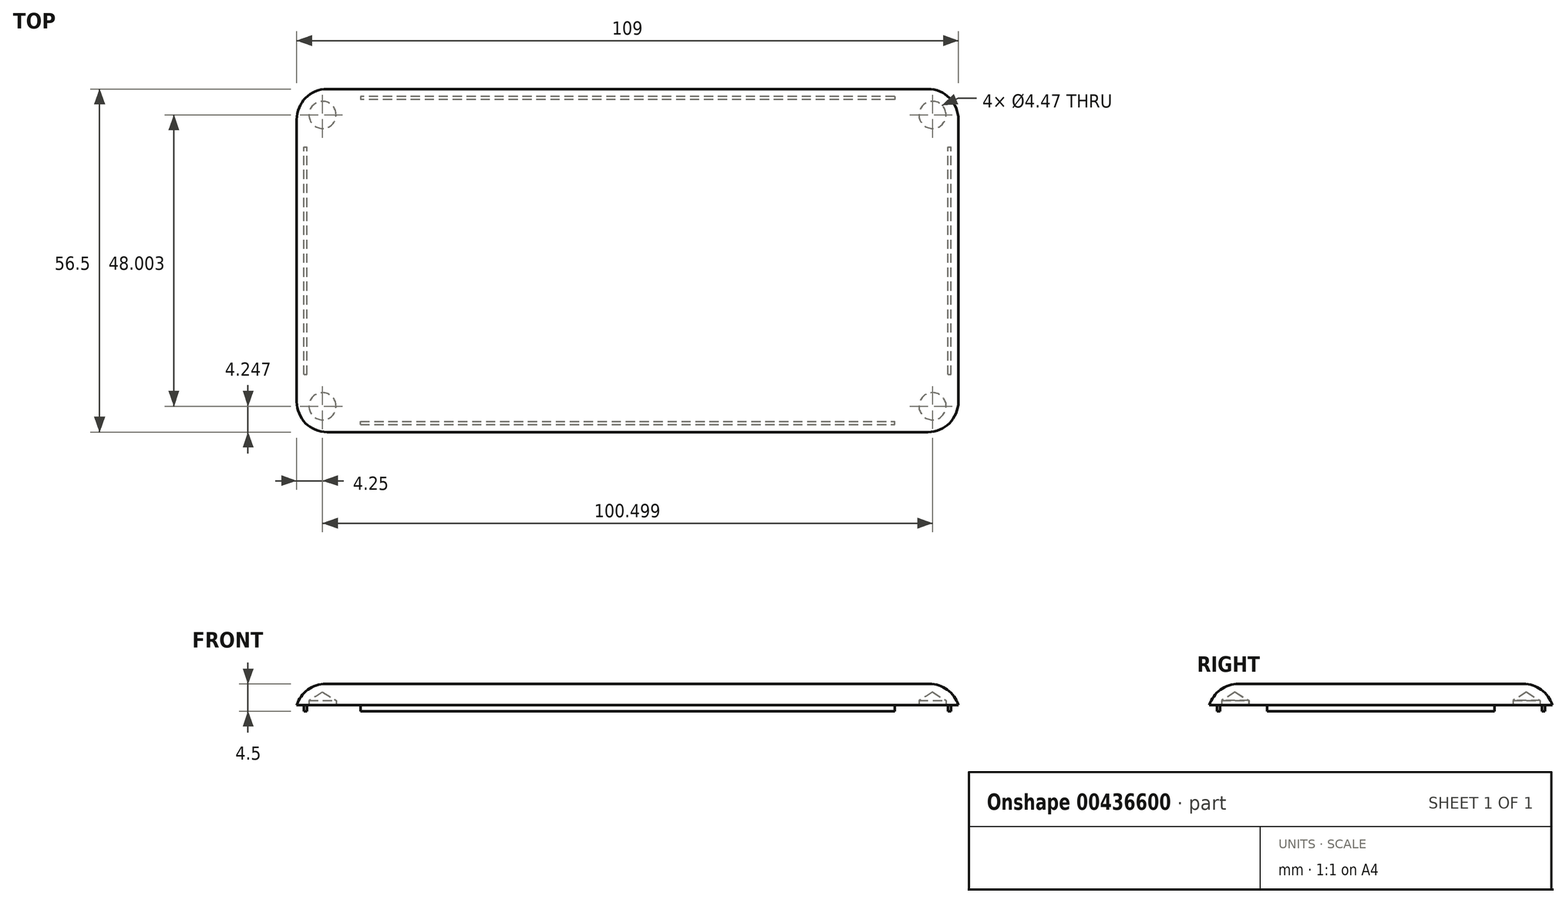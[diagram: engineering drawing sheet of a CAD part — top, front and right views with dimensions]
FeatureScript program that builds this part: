
annotation { "Feature Type Name" : "Feature", "Feature Type Description" : "" }
export const myFeature = defineFeature(function(context is Context, id is Id, definition is map)
    precondition{}
    {
        {
            var Q0;
            Q0=qCreatedBy(makeId("Top.planeOp"),FACE);
            var sketch = newSketch(context, id + "F0", { "sketchPlane" : qUnion([Q0])});
            skLineSegment(sketch, "E0.bottom", {"start": v(49.5, -28.25) * mm, "end": v(-49.5, -28.25) * mm});
            skLineSegment(sketch, "E0.top", {"start": v(49.5, 28.25) * mm, "end": v(-49.5, 28.25) * mm});
            skLineSegment(sketch, "E0.left", {"start": v(54.5, -23.25) * mm, "end": v(54.5, 23.25) * mm});
            skLineSegment(sketch, "E0.right", {"start": v(-54.5, -23.25) * mm, "end": v(-54.5, 23.25) * mm});
            skPoint(sketch, "E0.middle", {"position": v(0, 0) * mm});
            skPoint(sketch, "E1.visualSharp", {"position": v(-54.5, 28.25) * mm});
            skArc(sketch, "E1.filletArc", {"start": v(-49.5, 28.25) * mm, "mid": v(-53.04, 26.79) * mm, "end": v(-54.5, 23.25) * mm});
            skPoint(sketch, "E2.visualSharp", {"position": v(-53.42, 27.17) * mm});
            skPoint(sketch, "E3.visualSharp", {"position": v(-53.42, -27.17) * mm});
            skPoint(sketch, "E4.visualSharp", {"position": v(53.42, -27.17) * mm});
            skPoint(sketch, "E5.visualSharp", {"position": v(53.42, 27.17) * mm});
            skPoint(sketch, "E6.visualSharp", {"position": v(54.5, 28.25) * mm});
            skArc(sketch, "E6.filletArc", {"start": v(54.5, 23.25) * mm, "mid": v(53.04, 26.79) * mm, "end": v(49.5, 28.25) * mm});
            skPoint(sketch, "E7.visualSharp", {"position": v(54.5, -28.25) * mm});
            skArc(sketch, "E7.filletArc", {"start": v(49.5, -28.25) * mm, "mid": v(53.04, -26.79) * mm, "end": v(54.5, -23.25) * mm});
            skPoint(sketch, "E8.visualSharp", {"position": v(-54.5, -28.25) * mm});
            skArc(sketch, "E8.filletArc", {"start": v(-54.5, -23.25) * mm, "mid": v(-53.04, -26.79) * mm, "end": v(-49.5, -28.25) * mm});
            skSolve(sketch);
        }
        {
            var Q0;
            Q0=makeQuery(id+"F0.imprint","IMPRINT",FACE,{"disambiguationData":[TD([[makeQuery(id+"F0.imprint","IMPRINT",EDGE,{"derivedFrom":sQuery(id+"F0.wireOp",EDGE,"E0.bottom")}),-1.0]])]});
            extrude(context, id + "F1", {"entities" : qUnion([Q0]), "depth" : 3.5 * mm});
        }
        {
            var Q0;
            Q0=qCreatedBy(makeId("Top.planeOp"),FACE);
            var sketch = newSketch(context, id + "F2", { "sketchPlane" : qUnion([Q0])});
            skPoint(sketch, "E9.middle", {"position": v(-50.24, 24) * mm});
            skCircle(sketch, "E10", {"center": v(-50.24, 24) * mm, "radius": 2.24 * mm});
            skPoint(sketch, "E11.middle", {"position": v(50.25, -24) * mm});
            skCircle(sketch, "E12", {"center": v(50.25, -24) * mm, "radius": 2.24 * mm});
            skPoint(sketch, "E13.middle", {"position": v(50.24, 24) * mm});
            skCircle(sketch, "E14", {"center": v(50.24, 24) * mm, "radius": 2.24 * mm});
            skPoint(sketch, "E15.middle", {"position": v(-50.25, -24) * mm});
            skCircle(sketch, "E16", {"center": v(-50.25, -24) * mm, "radius": 2.24 * mm});
            skSolve(sketch);
        }
        {
            var Q0;
            Q0=qCreatedBy(makeId("Top.planeOp"),FACE);
            var sketch = newSketch(context, id + "F3", { "sketchPlane" : qUnion([Q0])});
            skLineSegment(sketch, "E17.bottom", {"start": v(49.5, -28.25) * mm, "end": v(-49.5, -28.25) * mm});
            skLineSegment(sketch, "E17.top", {"start": v(49.5, 28.25) * mm, "end": v(-49.5, 28.25) * mm});
            skLineSegment(sketch, "E17.left", {"start": v(54.5, -23.25) * mm, "end": v(54.5, 23.25) * mm});
            skLineSegment(sketch, "E17.right", {"start": v(-54.5, -23.25) * mm, "end": v(-54.5, 23.25) * mm});
            skPoint(sketch, "E17.middle", {"position": v(0, 0) * mm});
            skPoint(sketch, "E18.visualSharp", {"position": v(-54.5, 28.25) * mm});
            skArc(sketch, "E18.filletArc", {"start": v(-49.5, 28.25) * mm, "mid": v(-53.04, 26.79) * mm, "end": v(-54.5, 23.25) * mm});
            skPoint(sketch, "E19.visualSharp", {"position": v(-53.42, 27.17) * mm});
            skPoint(sketch, "E20.visualSharp", {"position": v(-53.42, -27.17) * mm});
            skPoint(sketch, "E21.visualSharp", {"position": v(53.42, -27.17) * mm});
            skPoint(sketch, "E22.visualSharp", {"position": v(53.42, 27.17) * mm});
            skPoint(sketch, "E23.visualSharp", {"position": v(54.5, 28.25) * mm});
            skArc(sketch, "E23.filletArc", {"start": v(54.5, 23.25) * mm, "mid": v(53.04, 26.79) * mm, "end": v(49.5, 28.25) * mm});
            skPoint(sketch, "E24.visualSharp", {"position": v(54.5, -28.25) * mm});
            skArc(sketch, "E24.filletArc", {"start": v(49.5, -28.25) * mm, "mid": v(53.04, -26.79) * mm, "end": v(54.5, -23.25) * mm});
            skPoint(sketch, "E25.visualSharp", {"position": v(-54.5, -28.25) * mm});
            skArc(sketch, "E25.filletArc", {"start": v(-54.5, -23.25) * mm, "mid": v(-53.04, -26.79) * mm, "end": v(-49.5, -28.25) * mm});
            skLineSegment(sketch, "E26.bottom", {"start": v(48.42, 27.17) * mm, "end": v(-48.42, 27.17) * mm});
            skLineSegment(sketch, "E26.top", {"start": v(48.42, -27.17) * mm, "end": v(-48.42, -27.17) * mm});
            skLineSegment(sketch, "E26.left", {"start": v(53.42, 22.17) * mm, "end": v(53.42, -22.17) * mm});
            skLineSegment(sketch, "E26.right", {"start": v(-53.42, 22.17) * mm, "end": v(-53.42, -22.17) * mm});
            skArc(sketch, "E27.filletArc", {"start": v(-48.42, 27.17) * mm, "mid": v(-51.96, 25.7) * mm, "end": v(-53.42, 22.17) * mm});
            skArc(sketch, "E28.filletArc", {"start": v(-53.42, -22.17) * mm, "mid": v(-51.96, -25.7) * mm, "end": v(-48.42, -27.17) * mm});
            skArc(sketch, "E29.filletArc", {"start": v(48.42, -27.17) * mm, "mid": v(51.96, -25.7) * mm, "end": v(53.42, -22.17) * mm});
            skArc(sketch, "E30.filletArc", {"start": v(53.42, 22.17) * mm, "mid": v(51.96, 25.7) * mm, "end": v(48.42, 27.17) * mm});
            skSolve(sketch);
        }
        {
            var Q0;
            Q0=qCreatedBy(makeId("Top.planeOp"),FACE);
            var sketch = newSketch(context, id + "F4", { "sketchPlane" : qUnion([Q0])});
            skLineSegment(sketch, "E31.bottom", {"start": v(-51, 19.75) * mm, "end": v(-54.5, 19.75) * mm});
            skLineSegment(sketch, "E31.top", {"start": v(-46, 28.25) * mm, "end": v(-49.5, 28.25) * mm});
            skLineSegment(sketch, "E31.left", {"start": v(-46, 24.75) * mm, "end": v(-46, 28.25) * mm});
            skLineSegment(sketch, "E31.right", {"start": v(-54.5, 19.75) * mm, "end": v(-54.5, 23.25) * mm});
            skPoint(sketch, "E31.middle", {"position": v(-50.24, 24) * mm});
            skCircle(sketch, "E32", {"center": v(-50.24, 24) * mm, "radius": 2.24 * mm});
            skLineSegment(sketch, "E33.bottom", {"start": v(49.5, -28.25) * mm, "end": v(46, -28.25) * mm});
            skLineSegment(sketch, "E33.top", {"start": v(54.5, -19.75) * mm, "end": v(51, -19.75) * mm});
            skLineSegment(sketch, "E33.left", {"start": v(54.5, -23.25) * mm, "end": v(54.5, -19.75) * mm});
            skLineSegment(sketch, "E33.right", {"start": v(46, -28.25) * mm, "end": v(46, -24.75) * mm});
            skPoint(sketch, "E33.middle", {"position": v(50.25, -24) * mm});
            skCircle(sketch, "E34", {"center": v(50.25, -24) * mm, "radius": 2.24 * mm});
            skLineSegment(sketch, "E35.bottom", {"start": v(54.5, 19.75) * mm, "end": v(51, 19.75) * mm});
            skLineSegment(sketch, "E35.top", {"start": v(49.5, 28.25) * mm, "end": v(46, 28.25) * mm});
            skLineSegment(sketch, "E35.left", {"start": v(54.5, 19.75) * mm, "end": v(54.5, 23.25) * mm});
            skLineSegment(sketch, "E35.right", {"start": v(46, 24.75) * mm, "end": v(46, 28.25) * mm});
            skPoint(sketch, "E35.middle", {"position": v(50.24, 24) * mm});
            skCircle(sketch, "E36", {"center": v(50.24, 24) * mm, "radius": 2.24 * mm});
            skLineSegment(sketch, "E37.bottom", {"start": v(-46, -28.25) * mm, "end": v(-49.5, -28.25) * mm});
            skLineSegment(sketch, "E37.top", {"start": v(-51, -19.75) * mm, "end": v(-54.5, -19.75) * mm});
            skLineSegment(sketch, "E37.left", {"start": v(-46, -28.25) * mm, "end": v(-46, -24.75) * mm});
            skLineSegment(sketch, "E37.right", {"start": v(-54.5, -23.25) * mm, "end": v(-54.5, -19.75) * mm});
            skPoint(sketch, "E37.middle", {"position": v(-50.25, -24) * mm});
            skCircle(sketch, "E38", {"center": v(-50.25, -24) * mm, "radius": 2.24 * mm});
            skPoint(sketch, "E39.visualSharp", {"position": v(54.5, -28.25) * mm});
            skArc(sketch, "E39.filletArc", {"start": v(49.5, -28.25) * mm, "mid": v(53.03, -26.78) * mm, "end": v(54.5, -23.25) * mm});
            skPoint(sketch, "E40.visualSharp", {"position": v(46, -19.75) * mm});
            skArc(sketch, "E40.filletArc", {"start": v(51, -19.75) * mm, "mid": v(47.46, -21.21) * mm, "end": v(46, -24.75) * mm});
            skPoint(sketch, "E41.visualSharp", {"position": v(54.5, 28.25) * mm});
            skArc(sketch, "E41.filletArc", {"start": v(54.5, 23.25) * mm, "mid": v(53.03, 26.79) * mm, "end": v(49.5, 28.25) * mm});
            skPoint(sketch, "E42.visualSharp", {"position": v(46, 19.75) * mm});
            skArc(sketch, "E42.filletArc", {"start": v(46, 24.75) * mm, "mid": v(47.46, 21.21) * mm, "end": v(51, 19.75) * mm});
            skPoint(sketch, "E43.visualSharp", {"position": v(-46, 19.75) * mm});
            skArc(sketch, "E43.filletArc", {"start": v(-51, 19.75) * mm, "mid": v(-47.46, 21.21) * mm, "end": v(-46, 24.75) * mm});
            skPoint(sketch, "E44.visualSharp", {"position": v(-54.5, 28.25) * mm});
            skArc(sketch, "E44.filletArc", {"start": v(-49.5, 28.25) * mm, "mid": v(-53.03, 26.78) * mm, "end": v(-54.5, 23.25) * mm});
            skPoint(sketch, "E45.visualSharp", {"position": v(-54.5, -28.25) * mm});
            skArc(sketch, "E45.filletArc", {"start": v(-54.5, -23.25) * mm, "mid": v(-53.04, -26.79) * mm, "end": v(-49.5, -28.25) * mm});
            skPoint(sketch, "E46.visualSharp", {"position": v(-46, -19.75) * mm});
            skArc(sketch, "E46.filletArc", {"start": v(-46, -24.75) * mm, "mid": v(-47.46, -21.22) * mm, "end": v(-51, -19.75) * mm});
            skSolve(sketch);
        }
        {
            var Q0;
            Q0=sQuery(id+"F2.wireOp",VERTEX,"E9.middle");
            var Q1;
            Q1=sQuery(id+"F2.wireOp",VERTEX,"E15.middle");
            var Q2;
            Q2=sQuery(id+"F2.wireOp",VERTEX,"E11.middle");
            var Q3;
            Q3=sQuery(id+"F2.wireOp",VERTEX,"E13.middle");
            var Q4;
            Q4=makeQuery(id+"F1.opExtrude","SWEPT_BODY",BODY,{"disambiguationData":[OSD([sQuery(id+"F0.wireOp",EDGE,"E0.bottom"),sQuery(id+"F0.wireOp",EDGE,"E0.top"),sQuery(id+"F0.wireOp",EDGE,"E0.left"),sQuery(id+"F0.wireOp",EDGE,"E0.right"),sQuery(id+"F0.wireOp",EDGE,"E1.filletArc"),sQuery(id+"F0.wireOp",EDGE,"E6.filletArc"),sQuery(id+"F0.wireOp",EDGE,"E7.filletArc"),sQuery(id+"F0.wireOp",EDGE,"E8.filletArc")])]});
            hole(context, id + "F5", {"style" : HoleStyle.SIMPLE, "endStyle" : HoleEndStyle.BLIND, "oppositeDirection" : true, "holeDiameter" : 4.47 * mm, "holeDepth" : .8 * mm, "isTappedThrough" : true, "tappedDepth" : 12 * mm, "tapClearance" : 3, "locations" : qUnion([Q0, Q1, Q2, Q3]), "scope" : qUnion([Q4])});
        }
        {
            var Q0;
            Q0=makeQuery(id+"F1.opExtrude","CAP_EDGE",EDGE,{"disambiguationData":[OSD([sQuery(id+"F0.wireOp",EDGE,"E0.bottom")])],"isStart":false});
            fillet(context, id + "F6", {"entities" : qUnion([Q0]), "radius" : 5 * mm, "tangentPropagation" : true, "allowEdgeOverflow" : false});
        }
        {
            var Q0;
            Q0=qCreatedBy(makeId("Top.planeOp"),FACE);
            var sketch = newSketch(context, id + "F7", { "sketchPlane" : qUnion([Q0])});
            skLineSegment(sketch, "E47.bottom", {"start": v(52.3, -18.75) * mm, "end": v(53.3, -18.75) * mm});
            skLineSegment(sketch, "E47.top", {"start": v(52.3, 18.75) * mm, "end": v(53.3, 18.75) * mm});
            skLineSegment(sketch, "E47.left", {"start": v(52.3, -18.75) * mm, "end": v(52.3, 18.75) * mm});
            skLineSegment(sketch, "E47.right", {"start": v(53.3, -18.75) * mm, "end": v(53.3, 18.75) * mm});
            skPoint(sketch, "E47.middle", {"position": v(52.8, 0) * mm});
            skLineSegment(sketch, "E48.bottom", {"start": v(-44, -27.07) * mm, "end": v(44, -27.07) * mm});
            skLineSegment(sketch, "E48.top", {"start": v(-44, -26.07) * mm, "end": v(44, -26.07) * mm});
            skLineSegment(sketch, "E48.left", {"start": v(-44, -27.07) * mm, "end": v(-44, -26.07) * mm});
            skLineSegment(sketch, "E48.right", {"start": v(44, -27.07) * mm, "end": v(44, -26.07) * mm});
            skPoint(sketch, "E48.middle", {"position": v(0, -26.57) * mm});
            skLineSegment(sketch, "E49.bottom", {"start": v(44, 27.05) * mm, "end": v(-44, 27.05) * mm});
            skLineSegment(sketch, "E49.top", {"start": v(44, 26.05) * mm, "end": v(-44, 26.05) * mm});
            skLineSegment(sketch, "E49.left", {"start": v(44, 27.05) * mm, "end": v(44, 26.05) * mm});
            skLineSegment(sketch, "E49.right", {"start": v(-44, 27.05) * mm, "end": v(-44, 26.05) * mm});
            skPoint(sketch, "E49.middle", {"position": v(0, 26.55) * mm});
            skSolve(sketch);
        }
        {
            var Q0;
            Q0=qCreatedBy(makeId("Top.planeOp"),FACE);
            var sketch = newSketch(context, id + "F8", { "sketchPlane" : qUnion([Q0])});
            skLineSegment(sketch, "E50.bottom", {"start": v(-53.31, -18.76) * mm, "end": v(-52.81, -18.76) * mm});
            skLineSegment(sketch, "E50.top", {"start": v(-53.31, 18.74) * mm, "end": v(-52.81, 18.74) * mm});
            skLineSegment(sketch, "E50.left", {"start": v(-53.31, -18.76) * mm, "end": v(-53.31, 18.74) * mm});
            skLineSegment(sketch, "E50.right", {"start": v(-52.81, -18.76) * mm, "end": v(-52.81, 18.74) * mm});
            skPoint(sketch, "E50.middle", {"position": v(-53.06, -0.01) * mm});
            skLineSegment(sketch, "E51.bottom", {"start": v(52.82, -18.76) * mm, "end": v(53.32, -18.76) * mm});
            skLineSegment(sketch, "E51.top", {"start": v(52.82, 18.74) * mm, "end": v(53.32, 18.74) * mm});
            skLineSegment(sketch, "E51.left", {"start": v(52.82, -18.76) * mm, "end": v(52.82, 18.74) * mm});
            skLineSegment(sketch, "E51.right", {"start": v(53.32, -18.76) * mm, "end": v(53.32, 18.74) * mm});
            skPoint(sketch, "E51.middle", {"position": v(53.07, -0.01) * mm});
            skLineSegment(sketch, "E52.bottom", {"start": v(-44, -27) * mm, "end": v(44, -27) * mm});
            skLineSegment(sketch, "E52.top", {"start": v(-44, -26.5) * mm, "end": v(44, -26.5) * mm});
            skLineSegment(sketch, "E52.left", {"start": v(-44, -27) * mm, "end": v(-44, -26.5) * mm});
            skLineSegment(sketch, "E52.right", {"start": v(44, -27) * mm, "end": v(44, -26.5) * mm});
            skPoint(sketch, "E52.middle", {"position": v(0, -26.76) * mm});
            skLineSegment(sketch, "E53.bottom", {"start": v(44, 27.03) * mm, "end": v(-44, 27.03) * mm});
            skLineSegment(sketch, "E53.top", {"start": v(44, 26.53) * mm, "end": v(-44, 26.53) * mm});
            skLineSegment(sketch, "E53.left", {"start": v(44, 27.03) * mm, "end": v(44, 26.53) * mm});
            skLineSegment(sketch, "E53.right", {"start": v(-44, 27.03) * mm, "end": v(-44, 26.53) * mm});
            skPoint(sketch, "E53.middle", {"position": v(0, 26.78) * mm});
            skSolve(sketch);
        }
        {
            var Q0;
            Q0=makeQuery(id+"F8.imprint","IMPRINT",FACE,{"disambiguationData":[TD([[makeQuery(id+"F8.imprint","IMPRINT",EDGE,{"derivedFrom":sQuery(id+"F8.wireOp",EDGE,"E50.bottom")}),1.0]])]});
            var Q1;
            Q1=makeQuery(id+"F8.imprint","IMPRINT",FACE,{"disambiguationData":[TD([[makeQuery(id+"F8.imprint","IMPRINT",EDGE,{"derivedFrom":sQuery(id+"F8.wireOp",EDGE,"E52.bottom")}),1.0]])]});
            var Q2;
            Q2=makeQuery(id+"F8.imprint","IMPRINT",FACE,{"disambiguationData":[TD([[makeQuery(id+"F8.imprint","IMPRINT",EDGE,{"derivedFrom":sQuery(id+"F8.wireOp",EDGE,"E51.bottom")}),1.0]])]});
            var Q3;
            Q3=makeQuery(id+"F8.imprint","IMPRINT",FACE,{"disambiguationData":[TD([[makeQuery(id+"F8.imprint","IMPRINT",EDGE,{"derivedFrom":sQuery(id+"F8.wireOp",EDGE,"E53.bottom")}),1.0]])]});
            extrude(context, id + "F9", {"entities" : qUnion([Q0, Q1, Q2, Q3]), "operationType" : NewBodyOperationType.ADD, "oppositeDirection" : true, "depth" : 1 * mm});
        }
    });
